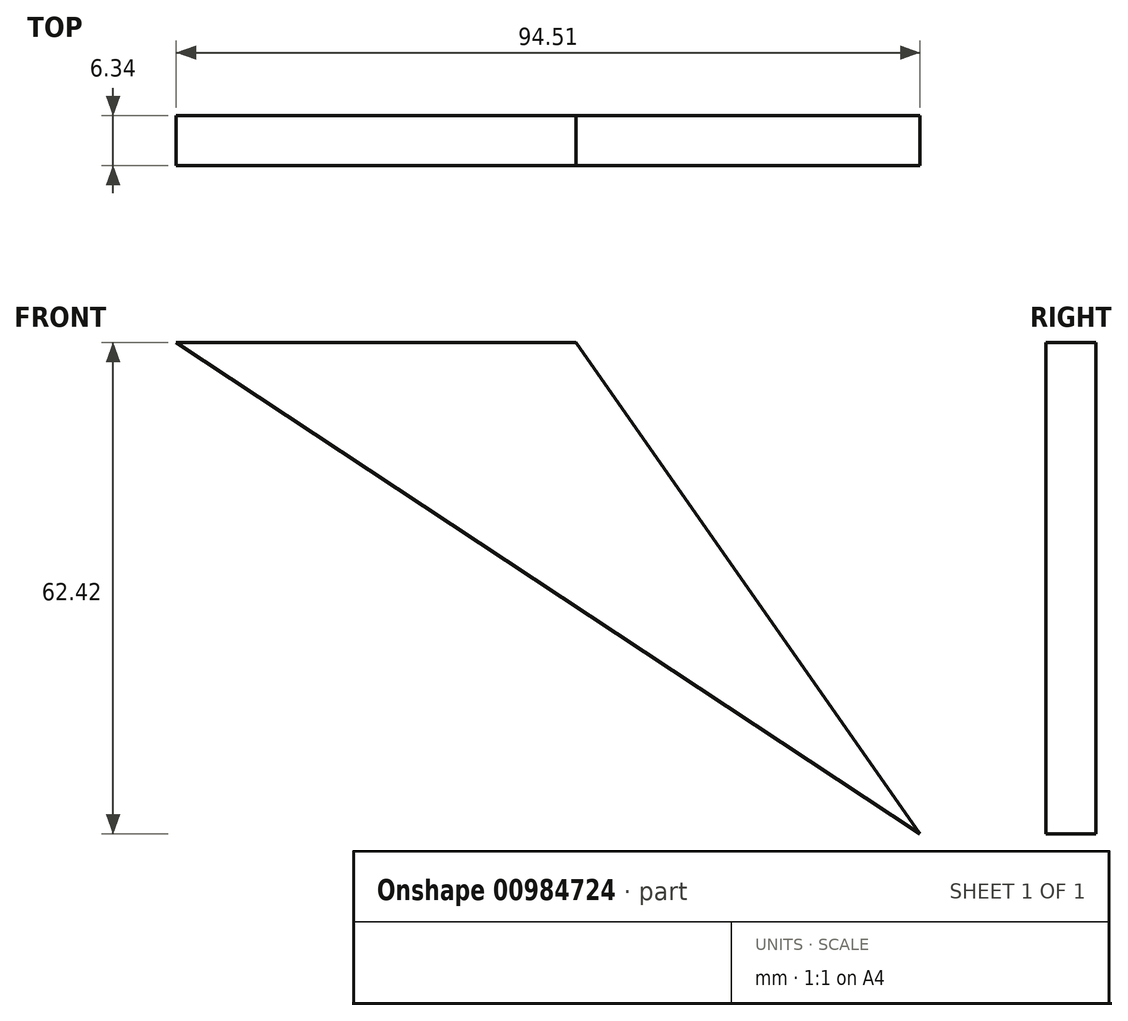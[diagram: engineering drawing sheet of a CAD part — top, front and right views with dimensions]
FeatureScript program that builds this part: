
annotation { "Feature Type Name" : "Feature", "Feature Type Description" : "" }
export const myFeature = defineFeature(function(context is Context, id is Id, definition is map)
    precondition{}
    {
        {
            var Q0;
            Q0=qCreatedBy(makeId("Front.planeOp"),FACE);
            var sketch = newSketch(context, id + "F0", { "sketchPlane" : qUnion([Q0])});
            skLineSegment(sketch, "E0", {"start": v(-34.43, 35.73) * mm, "end": v(16.37, 35.73) * mm});
            skLineSegment(sketch, "E1", {"start": v(16.37, 35.73) * mm, "end": v(60.08, -26.7) * mm});
            skLineSegment(sketch, "E2", {"start": v(-34.43, 35.73) * mm, "end": v(60.08, -26.7) * mm});
            skSolve(sketch);
        }
        {
            var Q0;
            Q0 = qSketchRegion(id + "F0", true);
            extrude(context, id + "F1", {"entities" : qUnion([Q0]), "depth" : 6.35 * mm, "offsetDistance" : 25.4 * mm, "symmetric" : true});
        }
    });
